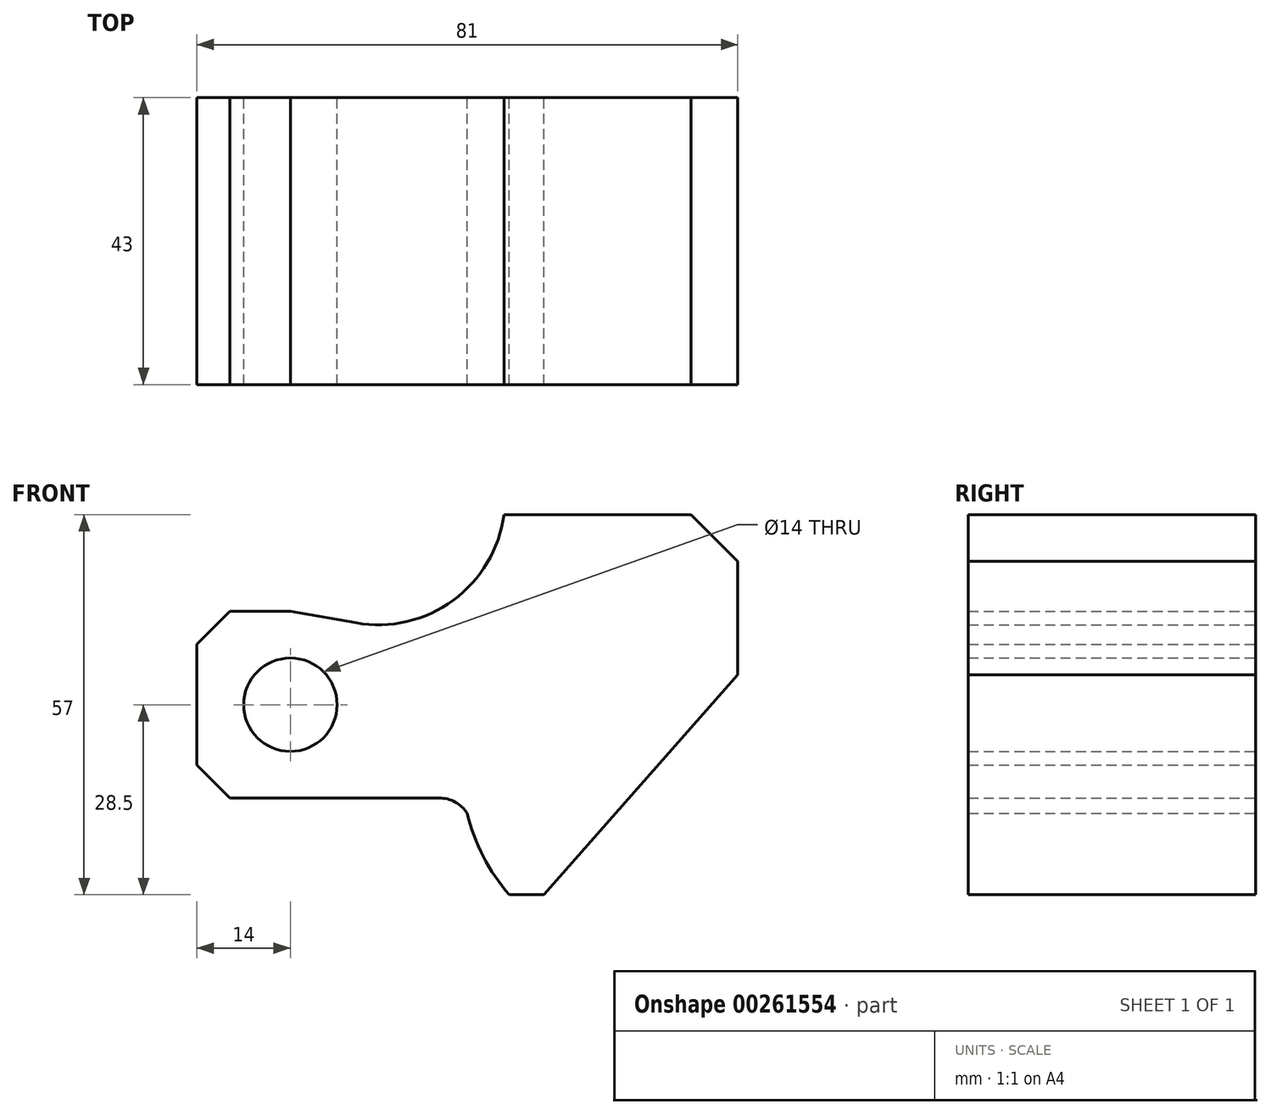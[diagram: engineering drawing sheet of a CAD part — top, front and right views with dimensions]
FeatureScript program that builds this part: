
annotation { "Feature Type Name" : "Feature", "Feature Type Description" : "" }
export const myFeature = defineFeature(function(context is Context, id is Id, definition is map)
    precondition{}
    {
        {
            var Q0;
            Q0=qCreatedBy(makeId("Front.planeOp"),FACE);
            var sketch = newSketch(context, id + "F0", { "sketchPlane" : qUnion([Q0])});
            skLineSegment(sketch, "E0.bottom", {"start": v(40.5, -28.5) * mm, "end": v(-40.5, -28.5) * mm});
            skLineSegment(sketch, "E0.top", {"start": v(40.5, 28.5) * mm, "end": v(-40.5, 28.5) * mm});
            skLineSegment(sketch, "E0.left", {"start": v(40.5, -28.5) * mm, "end": v(40.5, 28.5) * mm});
            skLineSegment(sketch, "E0.right", {"start": v(-40.5, -28.5) * mm, "end": v(-40.5, 28.5) * mm});
            skPoint(sketch, "E0.middle", {"position": v(0, 0) * mm});
            skLineSegment(sketch, "E1", {"start": v(40.5, 21.5) * mm, "end": v(33.5, 28.5) * mm});
            skLineSegment(sketch, "E2", {"start": v(40.5, 4.5) * mm, "end": v(11.5, -28.5) * mm});
            skPoint(sketch, "E3", {"position": v(28.2, -9.5) * mm});
            skLineSegment(sketch, "E4", {"start": v(28.2, -9.5) * mm, "end": v(28.2, -28.5) * mm});
            skArc(sketch, "E5", {"start": v(6.29, -28.5) * mm, "mid": v(2.4, -22.77) * mm, "end": v(0, -16.28) * mm});
            skPoint(sketch, "E6", {"position": v(5.5, 28.5) * mm});
            skCircle(sketch, "E7", {"center": v(-26.5, 0) * mm, "radius": 7 * mm});
            skLineSegment(sketch, "E8", {"start": v(-35.55, 14) * mm, "end": v(-26.5, 14) * mm});
            skLineSegment(sketch, "E9", {"start": v(-35.55, -14) * mm, "end": v(-26.5, -14) * mm});
            skLineSegment(sketch, "E10", {"start": v(-35.55, -14) * mm, "end": v(-40.5, -9.05) * mm});
            skLineSegment(sketch, "E11", {"start": v(-35.55, 14) * mm, "end": v(-40.5, 9.05) * mm});
            skLineSegment(sketch, "E12", {"start": v(-26.5, 14) * mm, "end": v(-16.64, 12.26) * mm});
            skArc(sketch, "E13", {"start": v(-16.64, 12.26) * mm, "mid": v(-2.1, 15.65) * mm, "end": v(5.5, 28.5) * mm});
            skLineSegment(sketch, "E14", {"start": v(-26.5, -14) * mm, "end": v(-4.2, -14) * mm});
            skArc(sketch, "E15", {"start": v(-4.2, -14) * mm, "mid": v(-1.8, -14.6) * mm, "end": v(0, -16.28) * mm});
            skSolve(sketch);
        }
        {
            var Q0;
            {var subQ4=sQuery(id+"F0.wireOp",EDGE,"E1");Q0=makeQuery(id+"F0.imprint","IMPRINT",FACE,{"disambiguationData":[TD([[makeQuery(id+"F0.imprint","IMPRINT",EDGE,{"derivedFrom":subQ4}),1.0]])]});}
            extrude(context, id + "F1", {"entities" : qUnion([Q0]), "depth" : 43 * mm});
        }
    });
